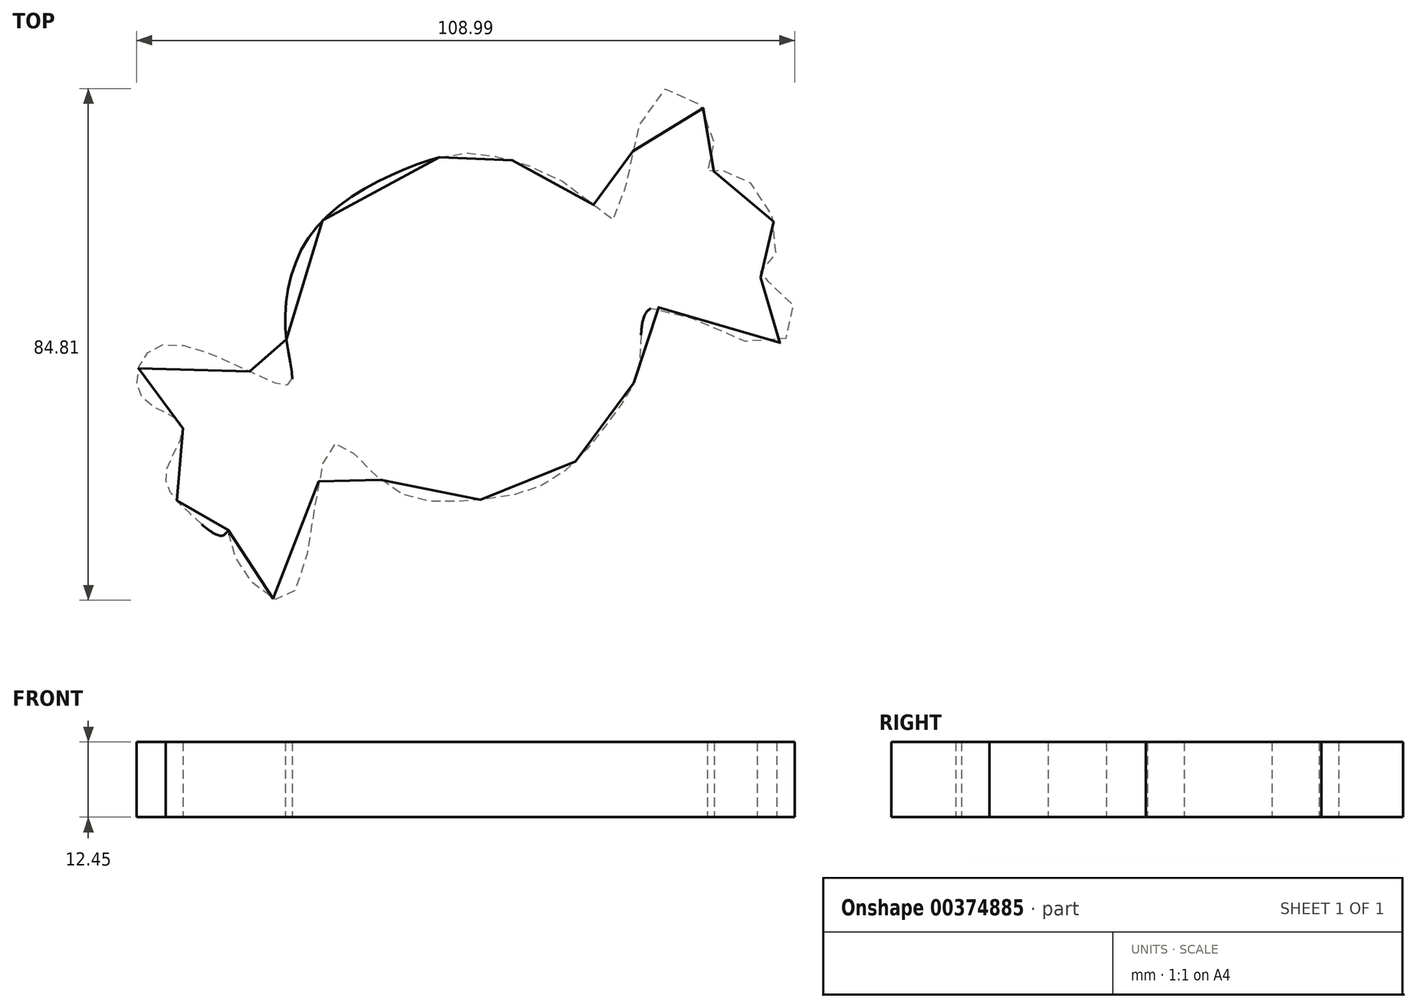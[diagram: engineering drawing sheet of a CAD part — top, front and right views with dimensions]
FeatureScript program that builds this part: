
annotation { "Feature Type Name" : "Feature", "Feature Type Description" : "" }
export const myFeature = defineFeature(function(context is Context, id is Id, definition is map)
    precondition{}
    {
        {
            var Q0;
            Q0=qCreatedBy(makeId("Top.planeOp"),FACE);
            var sketch = newSketch(context, id + "F0", { "sketchPlane" : qUnion([Q0])});
            skPoint(sketch, "E0.13.internal.snap0", {"position": v(58.04, -3.09) * mm});
            skPoint(sketch, "E0.29.internal.snap0", {"position": v(-49.43, -3.09) * mm});
            skPoint(sketch, "E0.31.internal.snap0", {"position": v(-49.43, -3.09) * mm});
            skFitSpline(sketch, "E0", {"points": [v(0, 27.99) * mm, v(6.39, 28.6) * mm, v(15.21, 26.47) * mm, v(25.25, 20.38) * mm, v(29.2, 17.95) * mm, v(36.2, 38.8) * mm, v(45.33, 32.86) * mm, v(44.42, 25.55) * mm, v(46.85, 25.86) * mm, v(54.15, 20.38) * mm, v(54.76, 10.04) * mm, v(52.63, 8.52) * mm, v(58.04, 4.56) * mm, v(55.37, -3.09) * mm, v(35.29, 3.04) * mm, v(33.16, -5.78) * mm, v(28.9, -14.6) * mm, v(18.56, -25.55) * mm, v(4.87, -28.9) * mm, v(-8.52, -26.47) * mm, v(-17.95, -19.77) * mm, v(-24.95, -44.98) * mm, v(-34.07, -37.72) * mm, v(-34.99, -33.77) * mm, v(-35.9, -34.68) * mm, v(-41.68, -30.73) * mm, v(-45.33, -24.34) * mm, v(-42.6, -16.43) * mm, v(-49.43, -11.56) * mm, v(-45.94, -3.09) * mm, v(-25.25, -9.74) * mm, v(-25.25, -3.09) * mm, v(-20.38, 16.43) * mm, v(0, 27.99) * mm]});
            skSolve(sketch);
        }
        {
            var Q0;
            Q0 = qSketchRegion(id + "F0", true);
            extrude(context, id + "F1", {"entities" : qUnion([Q0]), "depth" : 12.45 * mm});
        }
    });
